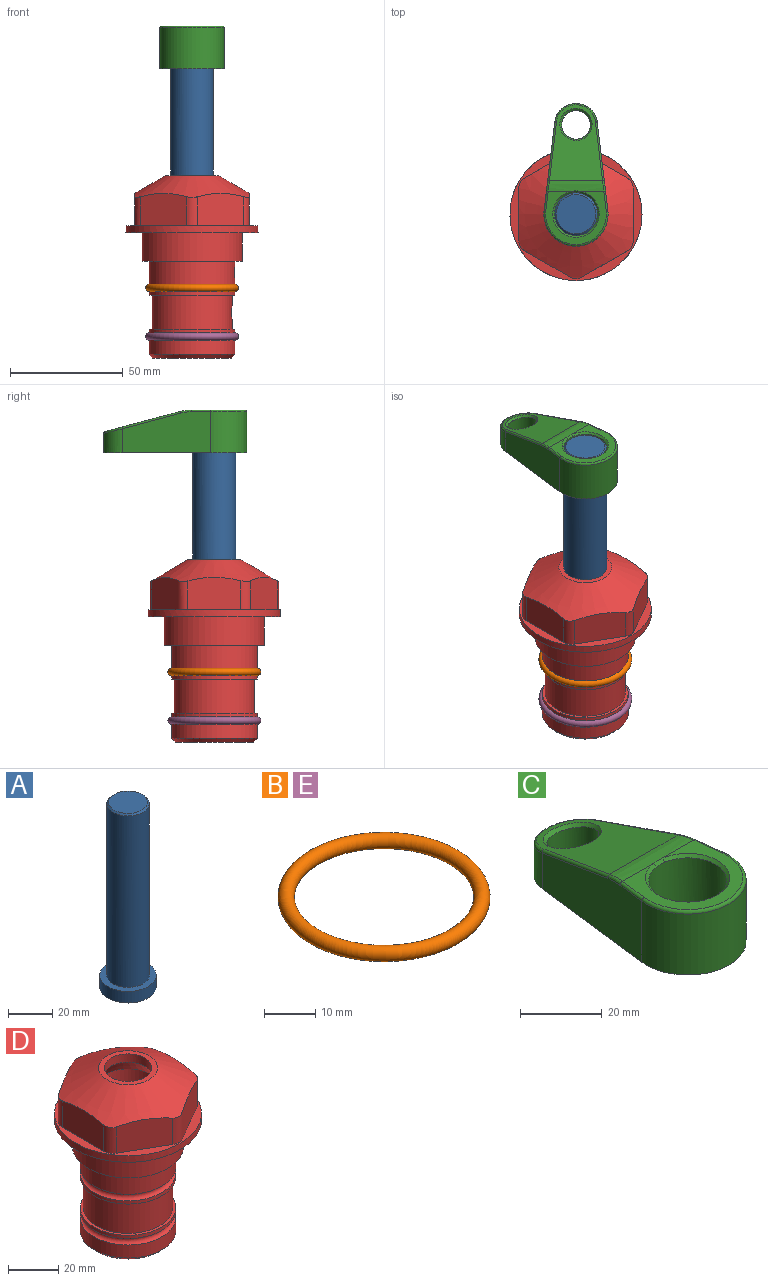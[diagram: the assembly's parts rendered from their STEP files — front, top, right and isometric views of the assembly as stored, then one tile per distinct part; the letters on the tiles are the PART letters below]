
ASSEMBLY  parts=5 mates=4
PART A: 6 faces, bbox 25.4x25.4x101.6 mm
  f0: plane 17.46x17.46mm, normal (0,0,1), area 239.5mm2, adj f5
  f1: plane 25.4x25.4mm, normal (0,0,-1), area 506.7mm2, adj f2
  f2: cylinder r=12.7mm len=25.4mm, axis (0,0,1), area 506.7mm2, adj f1,f3
  f3: plane 25.4x25.4mm, normal (0,0,1), area 221.7mm2, adj f2,f4
  f4: cylinder r=9.53mm len=94.46mm, axis (0,0,1), area 5653mm2, adj f3,f5
  f5: cone r=8.73mm half-angle=45deg, axis (0,0,-1), area 64.4mm2, adj f0,f4
PART B: 1 faces, bbox 44.7x44.7x3.2 mm
  f0: torus R=19.05mm, axis (0,0,1), area 1193.9mm2
PART C: 31 faces, bbox 31.7x65.5x19.8 mm
  f0: plane 39.12x18.26mm, normal (0.99,0.12,0), area 612.2mm2, adj f1,f4,f7,f11,f13,f15
  f1: cylinder r=9.53mm len=18.91mm, axis (0,0,-1), area 296.1mm2, adj f0,f2,f7,f17
  f2: plane 39.12x18.26mm, normal (-0.99,0.12,0), area 612.2mm2, adj f1,f4,f7,f12,f14,f16
  f3: cylinder r=6.35mm len=12.7mm, axis (0,0,-1), area 362.4mm2, adj f7,f18
  f4: cylinder r=14.29mm len=28.58mm, axis (0,0,-1), area 882.2mm2, adj f0,f2,f7,f10
  f5: cylinder r=9.53mm len=19.05mm, axis (0,0,-1), area 1092.6mm2, adj f7,f19,f20
  f6: plane 26.99x23.69mm, normal (0,0,1), area 216.2mm2, adj f9,f10,f11,f12,f19
  f7: plane 63.5x28.58mm, normal (0,0,-1), area 661.8mm2, adj f0,f1,f2,f3,f4,f5,f22,f23
  f8: plane 33.52x23.6mm, normal (0,0.26,0.97), area 486mm2, adj f9,f15,f16,f17,f18
  f9: cylinder r=19.05mm len=24.72mm, axis (1,0,0), area 120.4mm2, adj f6,f8,f13,f14,f20
  f10: torus R=13.49mm, axis (0,0,1), area 59mm2, adj f4,f6,f11,f12
  f11: cylinder r=0.79mm len=8.67mm, axis (0.12,-0.99,0), area 10.8mm2, adj f0,f6,f10,f13
  f12: cylinder r=0.79mm len=8.67mm, axis (0.12,0.99,0), area 10.8mm2, adj f2,f6,f10,f14
  f13: bspline ~4.95x1.42mm, area 6.1mm2, adj f0,f9,f11,f15
  f14: bspline ~4.95x1.42mm, area 6.1mm2, adj f2,f9,f12,f16
  f15: cylinder r=0.79mm len=25.95mm, axis (0.12,-0.96,0.26), area 32.9mm2, adj f0,f8,f13,f17
  f16: cylinder r=0.79mm len=25.95mm, axis (0.12,0.96,-0.26), area 32.9mm2, adj f2,f8,f14,f17
  f17: bspline ~18.91x8.38mm, area 30mm2, adj f1,f8,f15,f16
  f18: bspline ~14.29x14.29mm, area 48.3mm2, adj f3,f8
  f19: cone r=9.53mm half-angle=45deg, axis (0,0,1), area 66.5mm2, adj f5,f6,f20
  f20: bspline ~3.22x0.96mm, area 3.5mm2, adj f5,f9,f19
  f21: plane 2.75x2.72mm, normal (0,0,-1), area 2.9mm2, adj f23,f25,f28
  f22: plane 23.05x15.88mm, normal (-0.99,-0.12,0), area 323.6mm2, adj f7,f25,f26,f27,f28,f29
  f23: plane 23.05x15.88mm, normal (0.99,-0.12,0), area 323.6mm2, adj f7,f21,f25,f27,f28,f30
  f24: cylinder r=9.53mm len=10.69mm, axis (0,0,-1), area 114.7mm2, adj f7,f27,f29,f30
  f25: cylinder r=12.7mm len=20.59mm, axis (0,0,-1), area 381.1mm2, adj f7,f21,f22,f23,f26,f28
  f26: plane 2.75x2.72mm, normal (0,0,-1), area 2.9mm2, adj f22,f25,f28
  f27: plane 19.72x18.37mm, normal (0,-0.26,-0.97), area 291.8mm2, adj f22,f23,f24,f28,f29,f30
  f28: cylinder r=15.88mm len=19.92mm, axis (1,0,0), area 54.8mm2, adj f21,f22,f23,f25,f26,f27
  f29: cylinder r=1.59mm len=11mm, axis (0,0,-1), area 34.7mm2, adj f7,f22,f24,f27
  f30: cylinder r=1.59mm len=11mm, axis (0,0,-1), area 34.7mm2, adj f7,f23,f24,f27
PART D: 36 faces, bbox 58.7x58.7x81 mm
  f0: cylinder r=17.78mm len=35.56mm, axis (0,0,1), area 1670.8mm2, adj f23,f24,f31
  f1: cylinder r=19.05mm len=38.1mm, axis (0,0,1), area 1191.9mm2, adj f26,f27,f30
  f2: plane 58.66x58.66mm, normal (0,0,-1), area 1150.6mm2, adj f3,f28
  f3: cylinder r=29.33mm len=58.66mm, axis (0,0,-1), area 585.1mm2, adj f2,f4
  f4: plane 58.66x58.66mm, normal (0,0,1), area 475.9mm2, adj f3,f5,f6,f7,f8,f9,f10,f11
  f5: plane 20.32x14.34mm, normal (-0.5,0.87,0), area 324.4mm2, adj f4,f15,f16,f17
  f6: plane 20.32x14.34mm, normal (0.5,0.87,0), area 324.4mm2, adj f4,f14,f15,f17
  f7: plane 23.48x14.34mm, normal (1,0,0), area 324.4mm2, adj f4,f13,f14,f17
  f8: plane 20.32x14.34mm, normal (0.5,-0.87,0), area 324.4mm2, adj f4,f12,f13,f17
  f9: plane 20.32x14.34mm, normal (-0.5,-0.87,0), area 324.4mm2, adj f4,f11,f12,f17
  f10: plane 23.48x14.34mm, normal (-1,0,0), area 324.4mm2, adj f4,f11,f16,f17
  f11: cylinder r=5.08mm len=12.85mm, axis (0,0,-1), area 67.2mm2, adj f4,f9,f10,f17
  f12: cylinder r=5.08mm len=12.85mm, axis (0,0,-1), area 67.2mm2, adj f4,f8,f9,f17
  f13: cylinder r=5.08mm len=12.85mm, axis (0,0,-1), area 67.2mm2, adj f4,f7,f8,f17
  f14: cylinder r=5.08mm len=12.85mm, axis (0,0,-1), area 67.2mm2, adj f4,f6,f7,f17
  f15: cylinder r=5.08mm len=12.85mm, axis (0,0,-1), area 67.2mm2, adj f4,f5,f6,f17
  f16: cylinder r=5.08mm len=12.85mm, axis (0,0,-1), area 67.2mm2, adj f4,f5,f10,f17
  f17: cone r=11.73mm half-angle=60deg, axis (0,0,-1), area 2071.8mm2, adj f5,f6,f7,f8,f9,f10,f11,f12
  f18: plane 23.46x23.46mm, normal (0,0,1), area 147.4mm2, adj f17,f35
  f19: plane 34.93x34.93mm, normal (0,0,-1), area 958mm2, adj f29
  f20: cylinder r=19.05mm len=38.1mm, axis (0,0,1), area 760.1mm2, adj f21,f29
  f21: torus R=19.05mm, axis (0,0,1), area 565.3mm2, adj f20,f22
  f22: cylinder r=19.05mm len=38.1mm, axis (0,0,1), area 190mm2, adj f21,f23
  f23: plane 38.1x38.1mm, normal (0,0,1), area 146.9mm2, adj f0,f22
  f24: plane 38.1x38.1mm, normal (0,0,-1), area 146.9mm2, adj f0,f25
  f25: cylinder r=19.05mm len=38.1mm, axis (0,0,1), area 190mm2, adj f24,f26
  f26: torus R=19.05mm, axis (0,0,1), area 565.3mm2, adj f1,f25
  f27: plane 44.45x44.45mm, normal (0,0,-1), area 411.7mm2, adj f1,f28
  f28: cylinder r=22.23mm len=44.45mm, axis (0,0,1), area 1773.5mm2, adj f2,f27
  f29: cone r=19.05mm half-angle=45deg, axis (0,0,1), area 257.5mm2, adj f19,f20
  f30: cylinder r=3.17mm len=6.75mm, axis (-1,0,0), area 128mm2, adj f1,f33
  f31: cylinder r=3.17mm len=6.35mm, axis (-1,0,0), area 102.5mm2, adj f0,f33
  f32: plane 25.4x25.4mm, normal (0,0,1), area 506.7mm2, adj f33
  f33: cylinder r=12.7mm len=66.42mm, axis (0,0,-1), area 5236.2mm2, adj f30,f31,f32,f34
  f34: cone r=9.53mm half-angle=30deg, axis (0,0,-1), area 443.4mm2, adj f33,f35
  f35: cylinder r=9.53mm len=19.05mm, axis (0,0,-1), area 240.9mm2, adj f18,f34
PART E: same geometry as B
PLACE A t=(0,0,27.55)mm
PLACE B at identity
PLACE C t=(0,0,28.35)mm
PLACE D at identity fixed
PLACE E t=(0,0,-21.59)mm
MATE fastened D.f0 <-> E.f0  axis (0,0,1) through (0,0,-46.1)mm
MATE fastened D.f0 <-> B.f0  axis (0,0,1) through (0,0,-24.51)mm
MATE fastened A.f2 <-> C.f4  axis (0,0,1) through (0,0,91.05)mm
MATE slider A.f2 <-> D.f0  axis (0,0,-1) through (0,0,-10.55)mm
